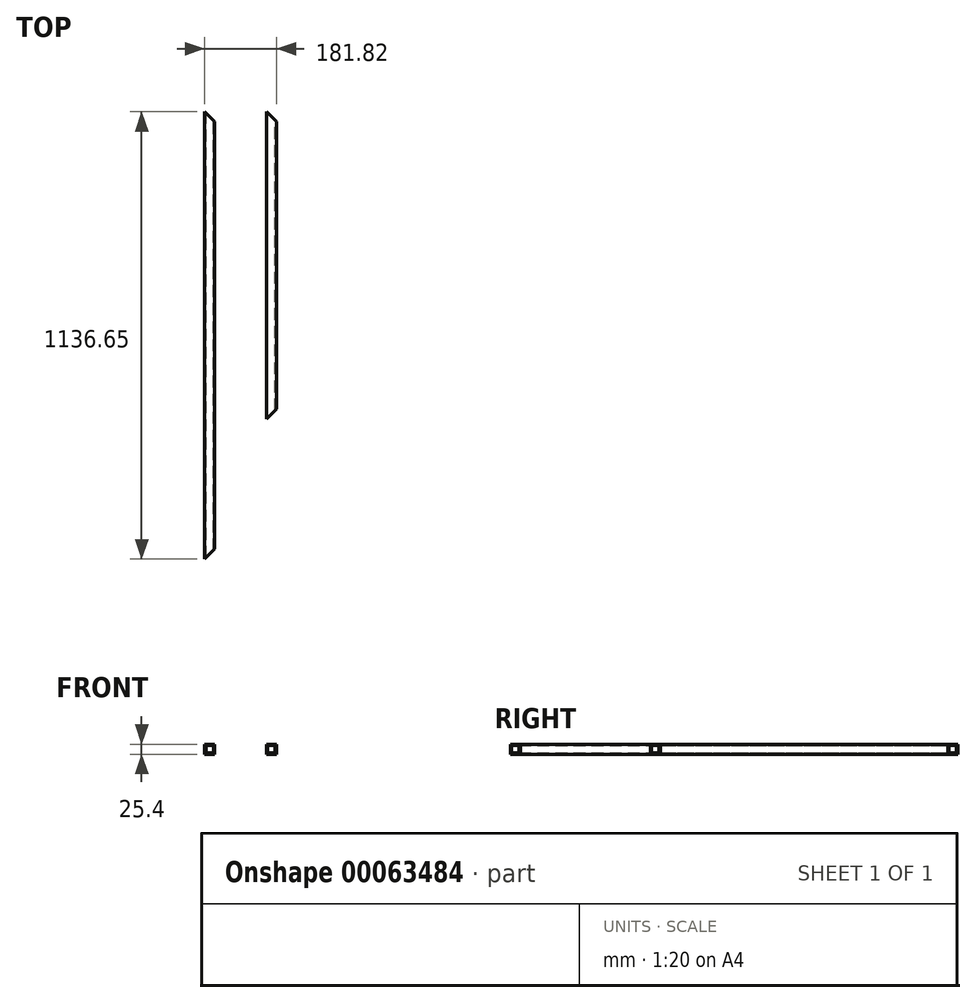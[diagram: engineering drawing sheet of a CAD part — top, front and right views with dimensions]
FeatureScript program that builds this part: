
annotation { "Feature Type Name" : "Feature", "Feature Type Description" : "" }
export const myFeature = defineFeature(function(context is Context, id is Id, definition is map)
    precondition{}
    {
        {
            var Q0;
            Q0=qCreatedBy(makeId("Front.planeOp"),FACE);
            var sketch = newSketch(context, id + "F0", { "sketchPlane" : qUnion([Q0])});
            skLineSegment(sketch, "E0.bottom", {"start": v(-109.17, 60.27) * mm, "end": v(-83.77, 60.27) * mm});
            skLineSegment(sketch, "E0.top", {"start": v(-109.17, 34.87) * mm, "end": v(-83.77, 34.87) * mm});
            skLineSegment(sketch, "E0.left", {"start": v(-109.17, 60.27) * mm, "end": v(-109.17, 34.87) * mm});
            skLineSegment(sketch, "E0.right", {"start": v(-83.77, 60.27) * mm, "end": v(-83.77, 34.87) * mm});
            skLineSegment(sketch, "E1.bottom", {"start": v(47.25, 60.27) * mm, "end": v(72.65, 60.27) * mm});
            skLineSegment(sketch, "E1.top", {"start": v(47.25, 34.87) * mm, "end": v(72.65, 34.87) * mm});
            skLineSegment(sketch, "E1.left", {"start": v(47.25, 60.27) * mm, "end": v(47.25, 34.87) * mm});
            skLineSegment(sketch, "E1.right", {"start": v(72.65, 60.27) * mm, "end": v(72.65, 34.87) * mm});
            skLineSegment(sketch, "E2.0", {"start": v(50.43, 57.1) * mm, "end": v(69.48, 57.1) * mm});
            skLineSegment(sketch, "E2.1", {"start": v(50.43, 57.1) * mm, "end": v(50.43, 38.05) * mm});
            skLineSegment(sketch, "E2.2", {"start": v(50.43, 38.05) * mm, "end": v(69.48, 38.05) * mm});
            skLineSegment(sketch, "E2.3", {"start": v(69.48, 57.1) * mm, "end": v(69.48, 38.05) * mm});
            skLineSegment(sketch, "E3.0", {"start": v(-106, 57.1) * mm, "end": v(-86.95, 57.1) * mm});
            skLineSegment(sketch, "E3.1", {"start": v(-106, 57.1) * mm, "end": v(-106, 38.05) * mm});
            skLineSegment(sketch, "E3.2", {"start": v(-106, 38.05) * mm, "end": v(-86.95, 38.05) * mm});
            skLineSegment(sketch, "E3.3", {"start": v(-86.95, 57.1) * mm, "end": v(-86.95, 38.05) * mm});
            skSolve(sketch);
        }
        {
            var Q0;
            Q0=makeQuery(id+"F0.imprint","IMPRINT",FACE,{"disambiguationData":[TD([[makeQuery(id+"F0.imprint","IMPRINT",EDGE,{"derivedFrom":sQuery(id+"F0.wireOp",EDGE,"E0.bottom")}),-1.0]])]});
            extrude(context, id + "F1", {"entities" : qUnion([Q0]), "depth" : 1136.65 * mm});
        }
        {
            var Q0;
            Q0=makeQuery(id+"F0.imprint","IMPRINT",FACE,{"disambiguationData":[TD([[makeQuery(id+"F0.imprint","IMPRINT",EDGE,{"derivedFrom":sQuery(id+"F0.wireOp",EDGE,"E1.bottom")}),-1.0]])]});
            extrude(context, id + "F2", {"entities" : qUnion([Q0]), "depth" : 781.05 * mm});
        }
        {
            var Q0;
            Q0=makeQuery(id+"F1.opExtrude","SWEPT_FACE",FACE,{"disambiguationData":[OSD([sQuery(id+"F0.wireOp",EDGE,"E0.bottom")])]});
            var sketch = newSketch(context, id + "F3", { "sketchPlane" : qUnion([Q0])});
            skLineSegment(sketch, "E4.0", {"start": v(-109.17, 0) * mm, "end": v(-83.77, 0) * mm});
            skLineSegment(sketch, "E4.1", {"start": v(-83.77, -1136.65) * mm, "end": v(-83.77, 0) * mm});
            skLineSegment(sketch, "E4.2", {"start": v(-109.17, -1136.65) * mm, "end": v(-109.17, 0) * mm});
            skLineSegment(sketch, "E4.3", {"start": v(-109.17, -1136.65) * mm, "end": v(-83.77, -1136.65) * mm});
            skLineSegment(sketch, "E4.4", {"start": v(47.25, -781.05) * mm, "end": v(47.25, 0) * mm});
            skLineSegment(sketch, "E4.5", {"start": v(47.25, -781.05) * mm, "end": v(72.65, -781.05) * mm});
            skLineSegment(sketch, "E4.6", {"start": v(72.65, -781.05) * mm, "end": v(72.65, 0) * mm});
            skLineSegment(sketch, "E4.7", {"start": v(47.25, 0) * mm, "end": v(72.65, 0) * mm});
            skLineSegment(sketch, "E5", {"start": v(47.25, 0) * mm, "end": v(72.65, -25.4) * mm});
            skLineSegment(sketch, "E6", {"start": v(-109.17, 0) * mm, "end": v(-83.77, -25.4) * mm});
            skLineSegment(sketch, "E7", {"start": v(47.25, -781.05) * mm, "end": v(72.65, -755.65) * mm});
            skLineSegment(sketch, "E8", {"start": v(-109.17, -1136.65) * mm, "end": v(-83.77, -1111.25) * mm});
            skSolve(sketch);
        }
        {
            var Q0;
            {var subQ0=sQuery(id+"F3.wireOp",EDGE,"E4.3");Q0=makeQuery(id+"F3.imprint","IMPRINT",FACE,{"disambiguationData":[TD([[makeQuery(id+"F3.imprint","IMPRINT",EDGE,{"derivedFrom":subQ0}),1.0]])]});}
            var Q1;
            {var subQ0=sQuery(id+"F3.wireOp",EDGE,"E4.5");Q1=makeQuery(id+"F3.imprint","IMPRINT",FACE,{"disambiguationData":[TD([[makeQuery(id+"F3.imprint","IMPRINT",EDGE,{"derivedFrom":subQ0}),1.0]])]});}
            var Q2;
            {var subQ0=sQuery(id+"F3.wireOp",EDGE,"E4.0");Q2=makeQuery(id+"F3.imprint","IMPRINT",FACE,{"disambiguationData":[TD([[makeQuery(id+"F3.imprint","IMPRINT",EDGE,{"derivedFrom":subQ0}),-1.0]])]});}
            var Q3;
            {var subQ0=sQuery(id+"F3.wireOp",EDGE,"E4.7");Q3=makeQuery(id+"F3.imprint","IMPRINT",FACE,{"disambiguationData":[TD([[makeQuery(id+"F3.imprint","IMPRINT",EDGE,{"derivedFrom":subQ0}),-1.0]])]});}
            extrude(context, id + "F4", {"entities" : qUnion([Q0, Q1, Q2, Q3]), "operationType" : NewBodyOperationType.REMOVE, "endBound" : BoundingType.THROUGH_ALL, "oppositeDirection" : true, "depth" : 25.4 * mm});
        }
    });
